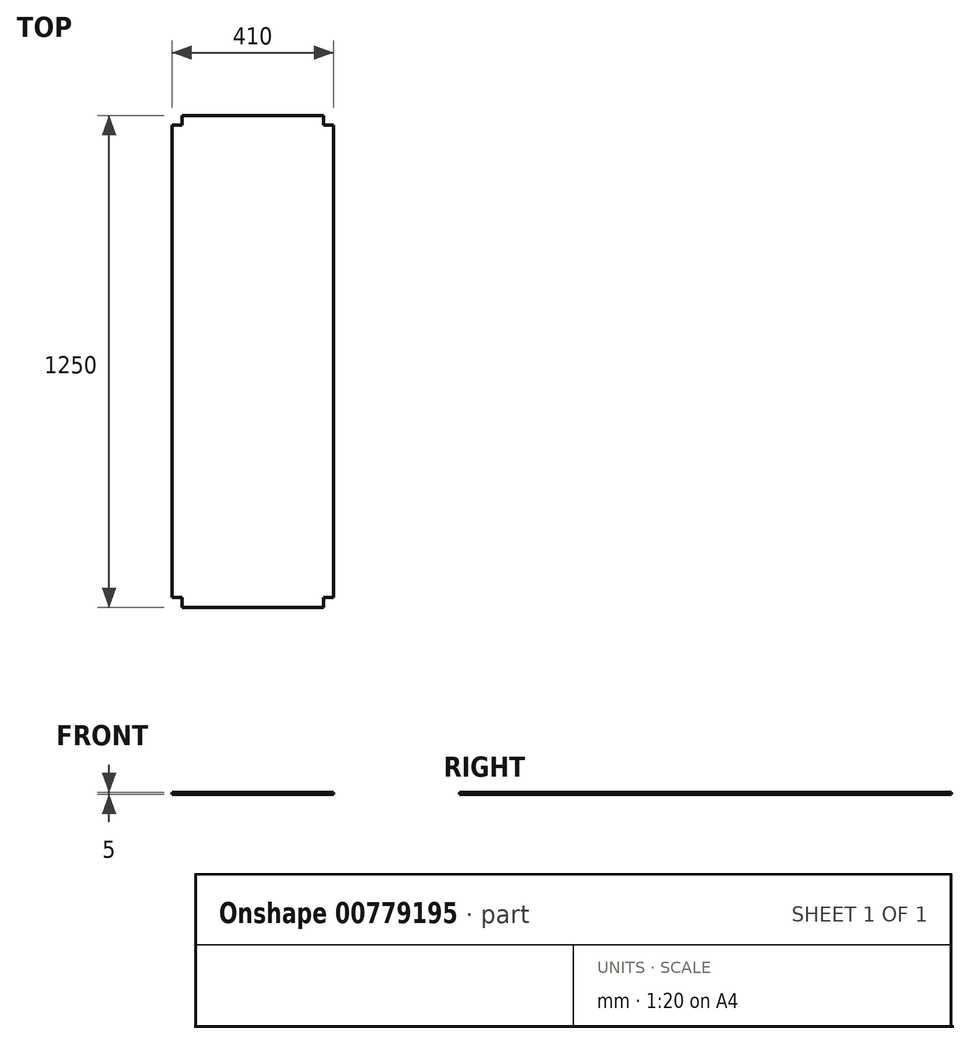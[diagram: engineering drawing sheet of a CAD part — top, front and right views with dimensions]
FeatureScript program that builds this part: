
annotation { "Feature Type Name" : "Feature", "Feature Type Description" : "" }
export const myFeature = defineFeature(function(context is Context, id is Id, definition is map)
    precondition{}
    {
        {
            var Q0;
            Q0=qCreatedBy(makeId("Top.planeOp"),FACE);
            var sketch = newSketch(context, id + "F0", { "sketchPlane" : qUnion([Q0])});
            skLineSegment(sketch, "E0.bottom", {"start": v(0, 0) * mm, "end": v(410, 0) * mm});
            skLineSegment(sketch, "E0.top", {"start": v(0, 1250) * mm, "end": v(410, 1250) * mm});
            skLineSegment(sketch, "E0.left", {"start": v(0, 0) * mm, "end": v(0, 1250) * mm});
            skLineSegment(sketch, "E0.right", {"start": v(410, 0) * mm, "end": v(410, 1250) * mm});
            skSolve(sketch);
        }
        {
            var Q0;
            Q0=qSketchRegion(id+"F0",true);
            extrude(context, id + "F1", {"entities" : qUnion([Q0]), "depth" : 5 * mm});
        }
        {
            var Q0;
            Q0=makeQuery(id+"F1.opExtrude","CAP_FACE",FACE,{"disambiguationData":[OSD([sQuery(id+"F0.wireOp",EDGE,"E0.bottom"),sQuery(id+"F0.wireOp",EDGE,"E0.top"),sQuery(id+"F0.wireOp",EDGE,"E0.left"),sQuery(id+"F0.wireOp",EDGE,"E0.right")])],"isStart":false});
            var sketch = newSketch(context, id + "F2", { "sketchPlane" : qUnion([Q0])});
            skLineSegment(sketch, "E1.bottom", {"start": v(0, 0) * mm, "end": v(25, 0) * mm});
            skLineSegment(sketch, "E1.top", {"start": v(0, 25) * mm, "end": v(25, 25) * mm});
            skLineSegment(sketch, "E1.left", {"start": v(0, 0) * mm, "end": v(0, 25) * mm});
            skLineSegment(sketch, "E1.right", {"start": v(25, 0) * mm, "end": v(25, 25) * mm});
            skSolve(sketch);
        }
        {
            var Q0;
            Q0=qSketchRegion(id+"F2",true);
            extrude(context, id + "F3", {"entities" : qUnion([Q0]), "operationType" : NewBodyOperationType.REMOVE, "oppositeDirection" : true, "depth" : 25 * mm});
        }
        {
            var Q0;
            Q0=makeQuery(id+"F1.opExtrude","CAP_FACE",FACE,{"disambiguationData":[OSD([sQuery(id+"F0.wireOp",EDGE,"E0.bottom"),sQuery(id+"F0.wireOp",EDGE,"E0.top"),sQuery(id+"F0.wireOp",EDGE,"E0.left"),sQuery(id+"F0.wireOp",EDGE,"E0.right")])],"isStart":false});
            var sketch = newSketch(context, id + "F4", { "sketchPlane" : qUnion([Q0])});
            skLineSegment(sketch, "E2.bottom", {"start": v(410, 0) * mm, "end": v(385, 0) * mm});
            skLineSegment(sketch, "E2.top", {"start": v(410, 25) * mm, "end": v(385, 25) * mm});
            skLineSegment(sketch, "E2.left", {"start": v(410, 0) * mm, "end": v(410, 25) * mm});
            skLineSegment(sketch, "E2.right", {"start": v(385, 0) * mm, "end": v(385, 25) * mm});
            skSolve(sketch);
        }
        {
            var Q0;
            Q0=qSketchRegion(id+"F4",true);
            extrude(context, id + "F5", {"entities" : qUnion([Q0]), "operationType" : NewBodyOperationType.REMOVE, "oppositeDirection" : true, "depth" : 25 * mm});
        }
        {
            var Q0;
            Q0=makeQuery(id+"F1.opExtrude","CAP_FACE",FACE,{"disambiguationData":[OSD([sQuery(id+"F0.wireOp",EDGE,"E0.bottom"),sQuery(id+"F0.wireOp",EDGE,"E0.top"),sQuery(id+"F0.wireOp",EDGE,"E0.left"),sQuery(id+"F0.wireOp",EDGE,"E0.right")])],"isStart":false});
            var sketch = newSketch(context, id + "F6", { "sketchPlane" : qUnion([Q0])});
            skLineSegment(sketch, "E3.bottom", {"start": v(410, 1250) * mm, "end": v(385, 1250) * mm});
            skLineSegment(sketch, "E3.top", {"start": v(410, 1225) * mm, "end": v(385, 1225) * mm});
            skLineSegment(sketch, "E3.left", {"start": v(410, 1250) * mm, "end": v(410, 1225) * mm});
            skLineSegment(sketch, "E3.right", {"start": v(385, 1250) * mm, "end": v(385, 1225) * mm});
            skSolve(sketch);
        }
        {
            var Q0;
            Q0=qSketchRegion(id+"F6",true);
            extrude(context, id + "F7", {"entities" : qUnion([Q0]), "operationType" : NewBodyOperationType.REMOVE, "oppositeDirection" : true, "depth" : 25 * mm});
        }
        {
            var Q0;
            Q0=makeQuery(id+"F1.opExtrude","CAP_FACE",FACE,{"disambiguationData":[OSD([sQuery(id+"F0.wireOp",EDGE,"E0.bottom"),sQuery(id+"F0.wireOp",EDGE,"E0.top"),sQuery(id+"F0.wireOp",EDGE,"E0.left"),sQuery(id+"F0.wireOp",EDGE,"E0.right")])],"isStart":false});
            var sketch = newSketch(context, id + "F8", { "sketchPlane" : qUnion([Q0])});
            skLineSegment(sketch, "E4.bottom", {"start": v(0, 1250) * mm, "end": v(25, 1250) * mm});
            skLineSegment(sketch, "E4.top", {"start": v(0, 1225) * mm, "end": v(25, 1225) * mm});
            skLineSegment(sketch, "E4.left", {"start": v(0, 1250) * mm, "end": v(0, 1225) * mm});
            skLineSegment(sketch, "E4.right", {"start": v(25, 1250) * mm, "end": v(25, 1225) * mm});
            skSolve(sketch);
        }
        {
            var Q0;
            Q0=makeQuery(id+"F8.imprint","IMPRINT",FACE,{"disambiguationData":[TD([[makeQuery(id+"F8.imprint","IMPRINT",EDGE,{"derivedFrom":sQuery(id+"F8.wireOp",EDGE,"E4.bottom")}),-1.0]])]});
            extrude(context, id + "F9", {"entities" : qUnion([Q0]), "operationType" : NewBodyOperationType.REMOVE, "oppositeDirection" : true, "depth" : 25 * mm});
        }
    });
